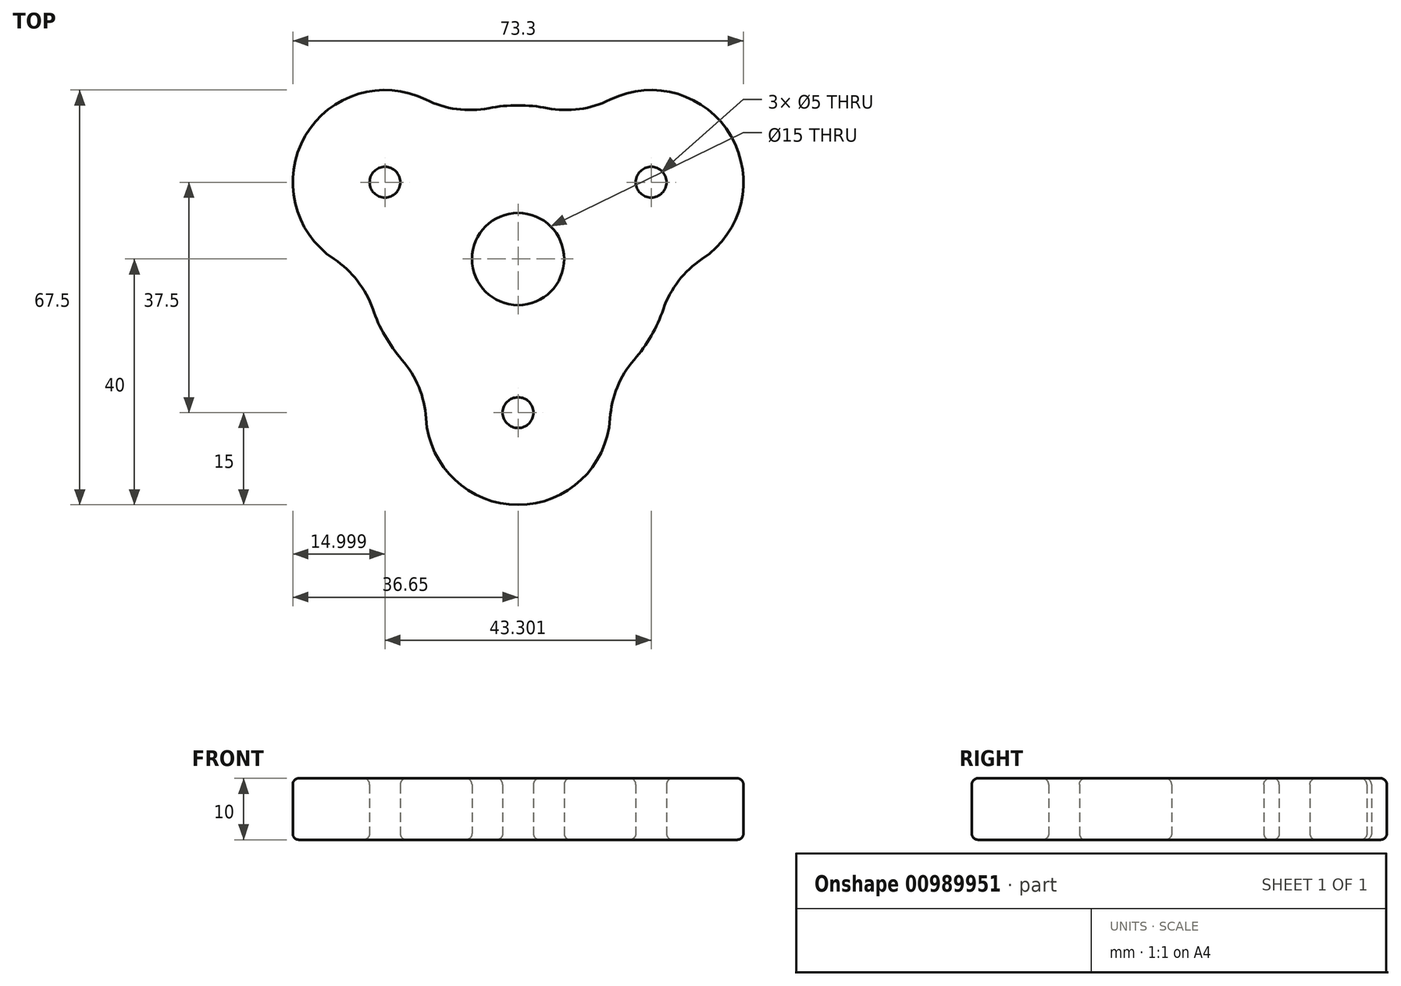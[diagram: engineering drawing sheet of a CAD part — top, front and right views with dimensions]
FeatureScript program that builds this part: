
annotation { "Feature Type Name" : "Feature", "Feature Type Description" : "" }
export const myFeature = defineFeature(function(context is Context, id is Id, definition is map)
    precondition{}
    {
        {
            var Q0;
            Q0=qCreatedBy(makeId("Top.planeOp"),FACE);
            var sketch = newSketch(context, id + "F0", { "sketchPlane" : qUnion([Q0])});
            skCircle(sketch, "E0", {"center": v(0, 0) * mm, "radius": 25 * mm, "construction": true});
            skLineSegment(sketch, "E1", {"start": v(0, 0) * mm, "end": v(-21.65, 12.5) * mm, "construction": true});
            skLineSegment(sketch, "E2", {"start": v(0, 0) * mm, "end": v(21.65, 12.5) * mm, "construction": true});
            skCircle(sketch, "E3", {"center": v(21.65, 12.5) * mm, "radius": 2.5 * mm});
            skCircle(sketch, "E4", {"center": v(-21.65, 12.5) * mm, "radius": 2.5 * mm});
            skCircle(sketch, "E5", {"center": v(0, -25) * mm, "radius": 2.5 * mm});
            skCircle(sketch, "E6", {"center": v(0, 0) * mm, "radius": 7.5 * mm});
            skArc(sketch, "E7", {"start": v(29.94, 0) * mm, "mid": v(34.64, 20) * mm, "end": v(14.97, 25.93) * mm});
            skArc(sketch, "E8.MirrorCS", {"start": v(-29.94, 0) * mm, "mid": v(-34.64, 20) * mm, "end": v(-14.97, 25.93) * mm});
            skArc(sketch, "E9", {"start": v(14.97, 25.93) * mm, "mid": v(9.98, 24.4) * mm, "end": v(4.76, 24.54) * mm});
            skArc(sketch, "E10.MirrorCS", {"start": v(-14.97, 25.93) * mm, "mid": v(-9.98, 24.4) * mm, "end": v(-4.76, 24.54) * mm});
            skArc(sketch, "E11", {"start": v(4.76, 24.54) * mm, "mid": v(0, 25) * mm, "end": v(-4.76, 24.54) * mm});
            skArc(sketch, "E12.MirrorCS", {"start": v(29.94, 0) * mm, "mid": v(26.12, -3.56) * mm, "end": v(23.63, -8.15) * mm});
            skArc(sketch, "E13.MirrorCS", {"start": v(-29.94, 0) * mm, "mid": v(-26.12, -3.56) * mm, "end": v(-23.63, -8.15) * mm});
            skLineSegment(sketch, "E14", {"start": v(0, 0) * mm, "end": v(-34.55, -19.95) * mm, "construction": true});
            skArc(sketch, "E15.MirrorCS", {"start": v(-14.97, -25.93) * mm, "mid": v(0, -40) * mm, "end": v(14.97, -25.93) * mm});
            skArc(sketch, "E16.MirrorCS", {"start": v(-14.97, -25.93) * mm, "mid": v(-16.14, -20.84) * mm, "end": v(-18.88, -16.4) * mm});
            skArc(sketch, "E17.MirrorCS", {"start": v(14.97, -25.93) * mm, "mid": v(16.14, -20.84) * mm, "end": v(18.88, -16.4) * mm});
            skArc(sketch, "E18", {"start": v(-23.63, -8.15) * mm, "mid": v(-21.65, -12.5) * mm, "end": v(-18.88, -16.4) * mm});
            skArc(sketch, "E19", {"start": v(23.63, -8.15) * mm, "mid": v(21.65, -12.5) * mm, "end": v(18.88, -16.4) * mm});
            skSolve(sketch);
        }
        {
            var Q0;
            Q0 = qSketchRegion(id + "F0", true);
            extrude(context, id + "F1", {"entities" : qUnion([Q0]), "depth" : 10 * mm, "offsetDistance" : 25 * mm});
        }
        {
            var Q0;
            Q0=makeQuery(id+"F1.opExtrude","CAP_EDGE",EDGE,{"disambiguationData":[OSD([sQuery(id+"F0.wireOp",EDGE,"E5")])],"isStart":true});
            var Q1;
            Q1=makeQuery(id+"F1.opExtrude","CAP_EDGE",EDGE,{"disambiguationData":[OSD([sQuery(id+"F0.wireOp",EDGE,"E6")])],"isStart":true});
            var Q2;
            Q2=makeQuery(id+"F1.opExtrude","CAP_EDGE",EDGE,{"disambiguationData":[OSD([sQuery(id+"F0.wireOp",EDGE,"E3")])],"isStart":true});
            var Q3;
            Q3=makeQuery(id+"F1.opExtrude","CAP_EDGE",EDGE,{"disambiguationData":[OSD([sQuery(id+"F0.wireOp",EDGE,"E4")])],"isStart":true});
            var Q4;
            Q4=makeQuery(id+"F1.opExtrude","CAP_EDGE",EDGE,{"disambiguationData":[OSD([sQuery(id+"F0.wireOp",EDGE,"E16.MirrorCS")])],"isStart":true});
            var Q5;
            Q5=makeQuery(id+"F1.opExtrude","CAP_EDGE",EDGE,{"disambiguationData":[OSD([sQuery(id+"F0.wireOp",EDGE,"E18")])],"isStart":false});
            var Q6;
            Q6=makeQuery(id+"F1.opExtrude","CAP_EDGE",EDGE,{"disambiguationData":[OSD([sQuery(id+"F0.wireOp",EDGE,"E5")])],"isStart":false});
            var Q7;
            Q7=makeQuery(id+"F1.opExtrude","CAP_EDGE",EDGE,{"disambiguationData":[OSD([sQuery(id+"F0.wireOp",EDGE,"E6")])],"isStart":false});
            var Q8;
            Q8=makeQuery(id+"F1.opExtrude","CAP_EDGE",EDGE,{"disambiguationData":[OSD([sQuery(id+"F0.wireOp",EDGE,"E3")])],"isStart":false});
            var Q9;
            Q9=makeQuery(id+"F1.opExtrude","CAP_EDGE",EDGE,{"disambiguationData":[OSD([sQuery(id+"F0.wireOp",EDGE,"E4")])],"isStart":false});
            fillet(context, id + "F2", {"entities" : qUnion([Q0, Q1, Q2, Q3, Q4, Q5, Q6, Q7, Q8, Q9]), "radius" : 1 * mm, "tangentPropagation" : true, "allowEdgeOverflow" : false});
        }
    });
